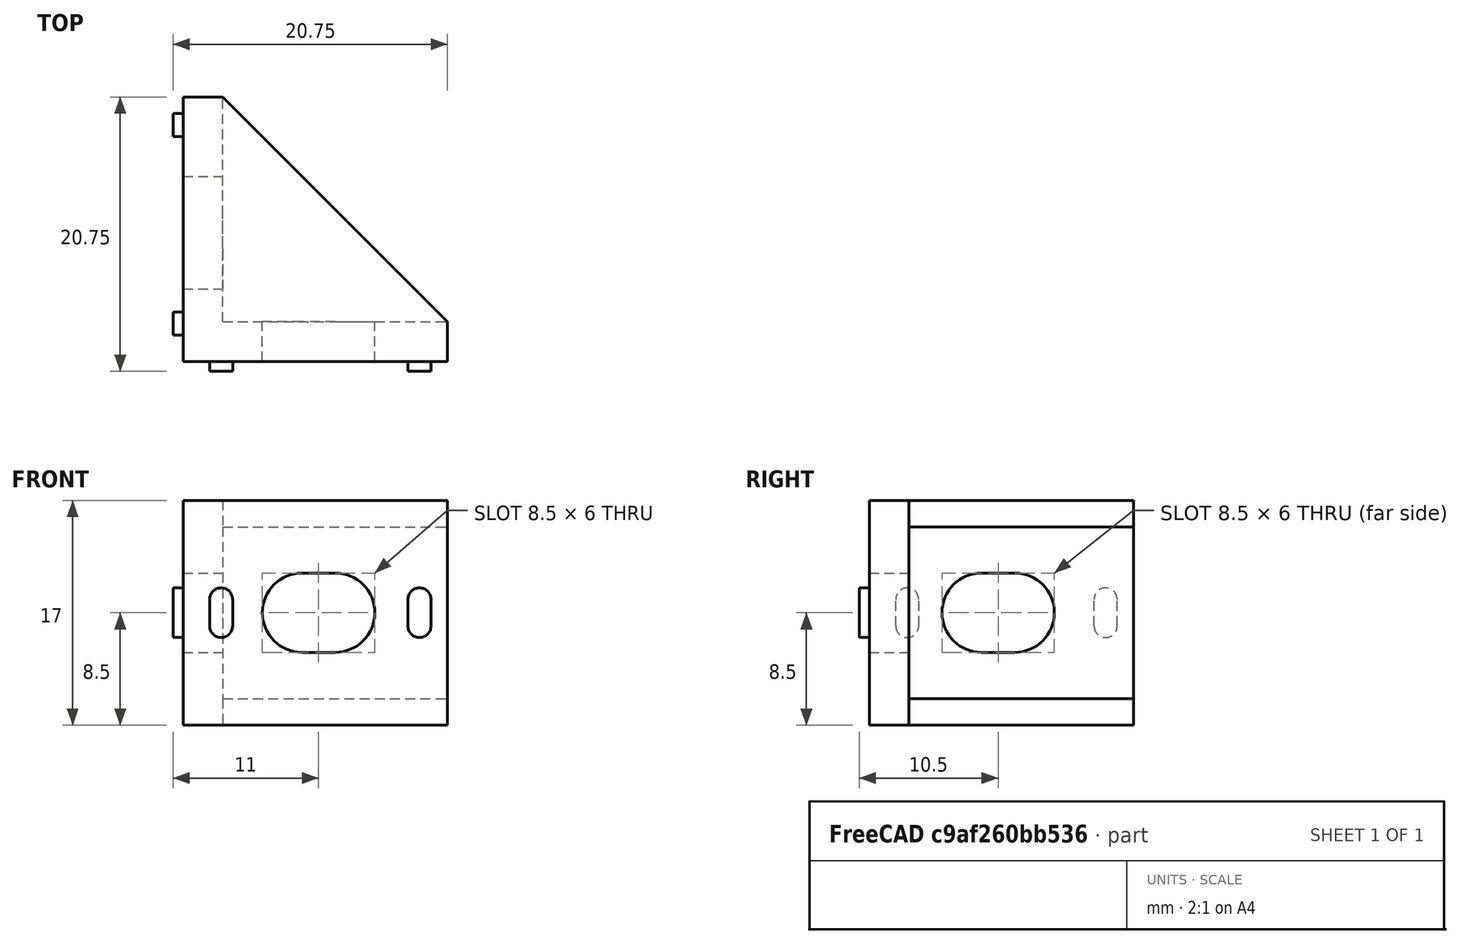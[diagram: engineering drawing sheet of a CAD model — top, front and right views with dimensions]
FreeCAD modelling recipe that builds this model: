
FCSTD DOCUMENT  (FreeCAD 0.18R14975 (Git))
Label: T-slot_20x20_90_joint
License: All rights reserved
LicenseURL: http://en.wikipedia.org/wiki/All_rights_reserved
objects: Part::Box×6, Part::Cylinder×6, Part::MultiFuse×6, Part::Feature×5, Part::Cut×4
note: 27 computed .brp shape members not serialized (recipe doc carries the construction recipe); baked Part::Feature solids carry a one-line shape summary decoded from their .brp

FEATURE [Part::Box] Box  label="Cube"
  AttacherType = Attacher::AttachEngine3D
  Height = 17
  Length = 20
  Width = 20
FEATURE [Part::Box] Box001  label="Cube001"
  AttacherType = Attacher::AttachEngine3D
  Height = 17
  Length = 15
  Placement = pos=(23,0,0) rot=(0,0,1;0.785398rad)
  Width = 30
FEATURE [Part::Cut] Cut
  Base = -> Box
  Tool = -> Box001
FEATURE [Part::Box] Box002  label="Cube002"
  AttacherType = Attacher::AttachEngine3D
  Height = 13
  Length = 20
  Placement = pos=(3,3,2) rot=(0,0,1;0rad)
  Width = 20
FEATURE [Part::Cut] Cut001
  Base = -> Cut
  Tool = -> Box002
FEATURE [Part::Cylinder] Cylinder
  Angle = 360
  AttacherType = Attacher::AttachEngine3D
  Height = 3
  Placement = pos=(-20,0,0) rot=(0,1,0;1.5708rad)
  Radius = 3
FEATURE [Part::Cylinder] Cylinder001
  Angle = 360
  AttacherType = Attacher::AttachEngine3D
  Height = 3
  Placement = pos=(-20,2.5,0) rot=(0,1,0;1.5708rad)
  Radius = 3
FEATURE [Part::Box] Box003  label="Cube003"
  AttacherType = Attacher::AttachEngine3D
  Height = 6
  Length = 3
  Placement = pos=(-20,0,-3) rot=(0,0,1;0rad)
  Width = 2.5
FEATURE [Part::Cylinder] Cylinder002
  Angle = 360
  AttacherType = Attacher::AttachEngine3D
  Height = 3
  Placement = pos=(-20,2.5,0) rot=(0,1,0;1.5708rad)
  Radius = 3
FEATURE [Part::Box] Box004  label="Cube004"
  AttacherType = Attacher::AttachEngine3D
  Height = 6
  Length = 3
  Placement = pos=(-20,0,-3) rot=(0,0,1;0rad)
  Width = 2.5
FEATURE [Part::Cylinder] Cylinder003
  Angle = 360
  AttacherType = Attacher::AttachEngine3D
  Height = 3
  Placement = pos=(-20,0,0) rot=(0,1,0;1.5708rad)
  Radius = 3
FEATURE [Part::MultiFuse] Fusion001
  Placement = pos=(11.5,20,8.5) rot=(0,0,1;1.5708rad)
  Shapes = -> [Box004,Cylinder002,Cylinder003]
FEATURE [Part::MultiFuse] Fusion
  Placement = pos=(20,8.5,8.5) rot=(0,0,1;0rad)
  Shapes = -> [Box003,Cylinder001,Cylinder]
FEATURE [Part::Cut] Cut002
  Base = -> Cut001
  Tool = -> Fusion
FEATURE [Part::Cut] Cut003
  Base = -> Cut002
  Tool = -> Fusion001
FEATURE [Part::Box] Box005  label="Cube005"
  AttacherType = Attacher::AttachEngine3D
  Height = 2.005
  Length = 1.75
  Placement = pos=(2,-0.75,7.495) rot=(0,0,1;0rad)
  Width = 0.75
FEATURE [Part::Cylinder] Cylinder004
  Angle = 360
  AttacherType = Attacher::AttachEngine3D
  Height = 0.75
  Placement = pos=(2.875,0,7.495) rot=(1,0,0;1.5708rad)
  Radius = 0.875
FEATURE [Part::Cylinder] Cylinder005
  Angle = 360
  AttacherType = Attacher::AttachEngine3D
  Height = 0.75
  Placement = pos=(2.875,0,9.5) rot=(1,0,0;1.5708rad)
  Radius = 0.875
FEATURE [Part::MultiFuse] Fusion002
  Shapes = -> [Cylinder005,Box005]
FEATURE [Part::MultiFuse] Fusion003
  Shapes = -> [Cylinder004,Fusion002]
FEATURE [Part::Feature] Fusion003001  label="Fusion004"
  shape: bbox 1.75 x 0.75 x 3.755 mm, 6 faces (baked)
FEATURE [Part::Feature] Fusion003002  label="Fusion005"
  Placement = pos=(15,0,0) rot=(0,0,1;0rad)
  shape: bbox 1.75 x 0.75 x 3.755 mm, 6 faces (baked)
FEATURE [Part::Feature] Fusion003003  label="Fusion006"
  Placement = pos=(-0.75,0,0) rot=(0,0,1;1.5708rad)
  shape: bbox 0.75 x 1.75 x 3.755 mm, 6 faces (baked)
FEATURE [Part::Feature] Fusion003004  label="Fusion007"
  Placement = pos=(-0.75,15,0) rot=(0,0,1;1.5708rad)
  shape: bbox 0.75 x 1.75 x 3.755 mm, 6 faces (baked)
FEATURE [Part::MultiFuse] Fusion003005
  Shapes = -> [Fusion003001,Fusion003004,Fusion003002,Fusion003003]
FEATURE [Part::MultiFuse] Fusion003006
  Shapes = -> [Fusion003005,Cut003]
FEATURE [Part::Feature] Fusion003006001  label="Fusion003007"
  shape: bbox 20.75 x 20.75 x 17 mm, 40 faces (baked)
